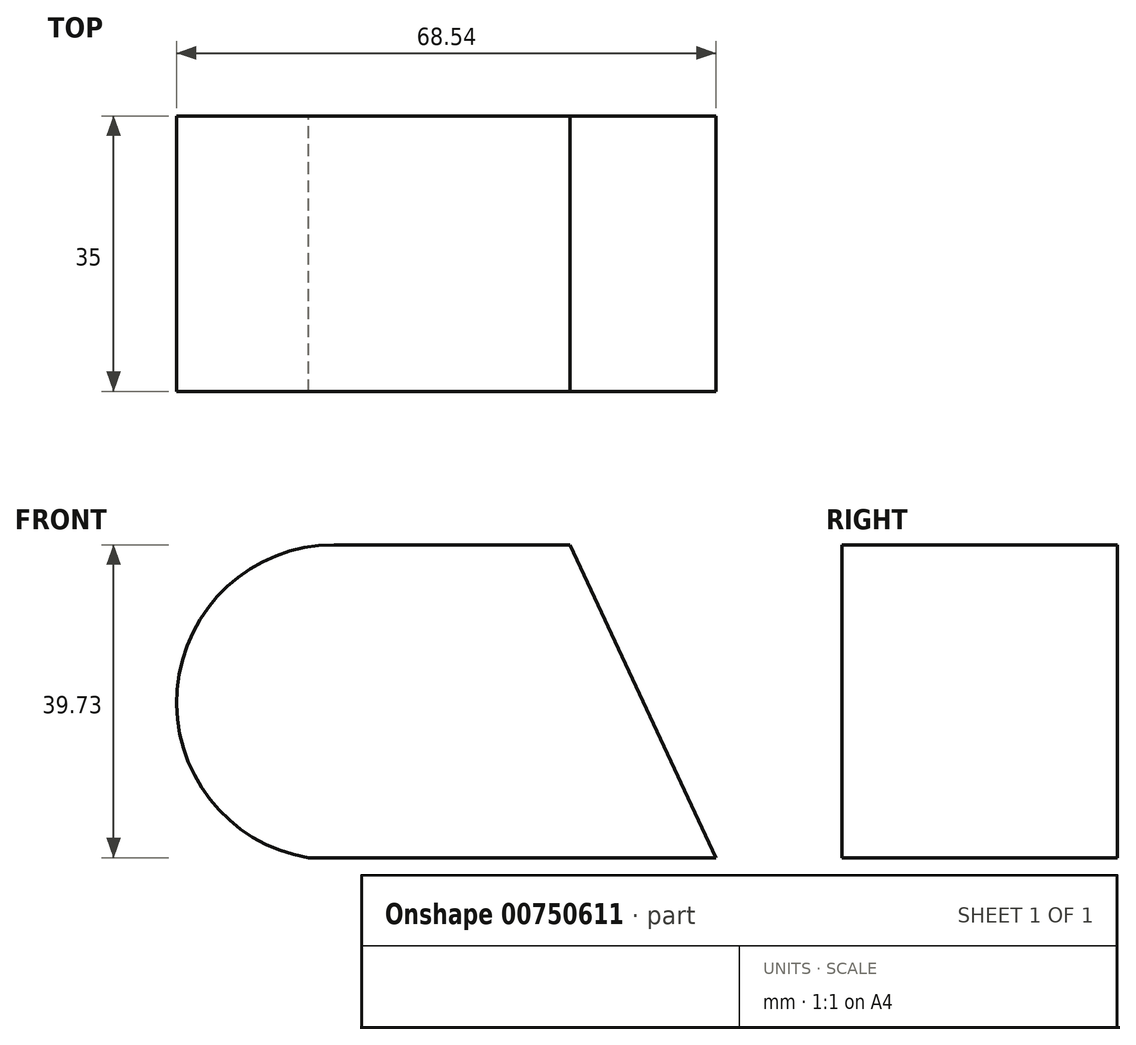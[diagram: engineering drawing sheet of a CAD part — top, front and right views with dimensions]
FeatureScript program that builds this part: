
annotation { "Feature Type Name" : "Feature", "Feature Type Description" : "" }
export const myFeature = defineFeature(function(context is Context, id is Id, definition is map)
    precondition{}
    {
        {
            var Q0;
            Q0=qCreatedBy(makeId("Front.planeOp"),FACE);
            var sketch = newSketch(context, id + "F0", { "sketchPlane" : qUnion([Q0])});
            skLineSegment(sketch, "E0", {"start": v(-10.11, 39.73) * mm, "end": v(19.89, 39.73) * mm});
            skLineSegment(sketch, "E1", {"start": v(-10.11, 0.99) * mm, "end": v(0, 39.73) * mm});
            skLineSegment(sketch, "E2", {"start": v(0, 39.73) * mm, "end": v(10, 39.73) * mm});
            skLineSegment(sketch, "E3", {"start": v(10, 39.73) * mm, "end": v(0, 0) * mm});
            skLineSegment(sketch, "E4", {"start": v(19.89, 39.73) * mm, "end": v(38.43, 0) * mm});
            skLineSegment(sketch, "E5", {"start": v(38.43, 0) * mm, "end": v(-13.37, 0) * mm});
            skArc(sketch, "E6", {"start": v(-10.11, 39.73) * mm, "mid": v(-30.05, 21.37) * mm, "end": v(-13.37, 0) * mm});
            skSolve(sketch);
        }
        {
            var Q0;
            Q0 = qSketchRegion(id + "F0", true);
            extrude(context, id + "F1", {"entities" : qUnion([Q0]), "depth" : 35 * mm, "offsetDistance" : 25 * mm});
        }
        {
            var Q0;
            Q0=makeQuery(id+"F1.opExtrude","SWEPT_FACE",FACE,{"disambiguationData":[OSD([sQuery(id+"F0.wireOp",EDGE,"E0"),sQuery(id+"F0.wireOp",EDGE,"E2")])]});
            var sketch = newSketch(context, id + "F2", { "sketchPlane" : qUnion([Q0])});
            skLineSegment(sketch, "E7.bottom", {"start": v(0, -35) * mm, "end": v(9.97, -35) * mm});
            skLineSegment(sketch, "E7.top", {"start": v(0, 0) * mm, "end": v(9.97, 0) * mm});
            skLineSegment(sketch, "E7.left", {"start": v(0, -35) * mm, "end": v(0, 0) * mm});
            skLineSegment(sketch, "E7.right", {"start": v(9.97, -35) * mm, "end": v(9.97, 0) * mm});
            skSolve(sketch);
        }
        {
            var Q0;
            Q0 = qSketchRegion(id + "F2", true);
            extrude(context, id + "F3", {"entities" : qUnion([Q0]), "operationType" : NewBodyOperationType.ADD, "oppositeDirection" : true, "depth" : 8 * mm, "offsetDistance" : 25 * mm});
        }
    });
